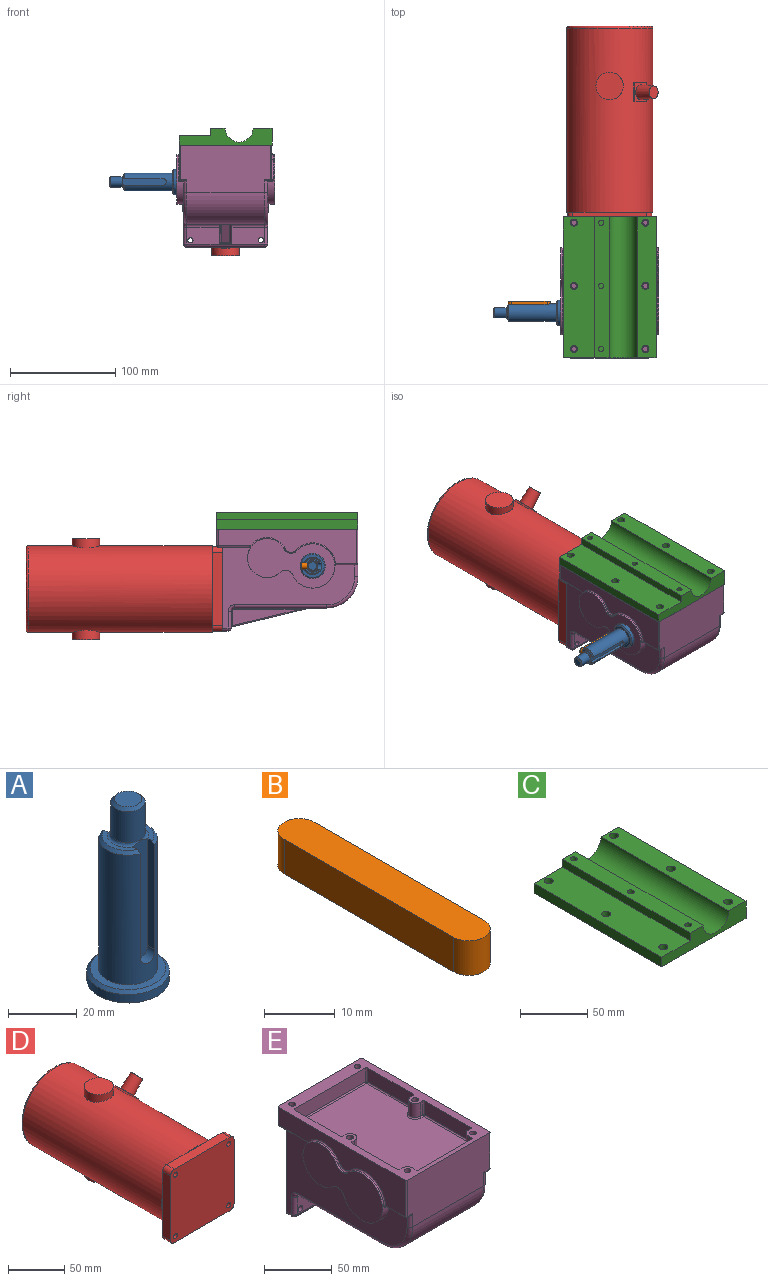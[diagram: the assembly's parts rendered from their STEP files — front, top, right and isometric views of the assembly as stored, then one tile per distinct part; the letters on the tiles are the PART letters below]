
ASSEMBLY  parts=5 mates=4
PART A: 21 faces, bbox 24x24x64 mm
  f0: plane 13.75x4.5mm, normal (0,0,1), area 22.7mm2, adj f10,f14,f18,f20
  f1: plane 13.75x4.5mm, normal (0,0,1), area 22.7mm2, adj f2,f12,f16,f20
  f2: cone r=7.5mm half-angle=45deg, axis (0,0,-1), area 26.8mm2, adj f1,f6,f12,f16
  f3: plane 24x24mm, normal (0,0,-1), area 452.4mm2, adj f4
  f4: cylinder r=12mm len=24mm, axis (0,0,1), area 226.2mm2, adj f3,f9
  f5: plane 22x22mm, normal (0,0,1), area 153.2mm2, adj f6,f9
  f6: cylinder r=8.5mm len=46mm, axis (0,0,1), area 1974.2mm2, adj f2,f5,f10,f12,f13,f14,f16,f17
  f7: cylinder r=4.98mm len=11mm, axis (0,0,1), area 344.2mm2, adj f11,f20
  f8: plane 7.96x7.96mm, normal (0,0,1), area 49.8mm2, adj f11
  f9: cone r=11mm half-angle=45deg, axis (0,0,-1), area 102.2mm2, adj f4,f5
  f10: cone r=7.5mm half-angle=45deg, axis (0,0,-1), area 26.8mm2, adj f0,f6,f14,f18
  f11: cone r=3.98mm half-angle=45deg, axis (0,0,-1), area 39.8mm2, adj f7,f8
  f12: plane 38.04x2.98mm, normal (1,0,0), area 111.7mm2, adj f1,f2,f6,f13,f15,f20
  f13: cylinder r=3mm len=6mm, axis (0,1,0), area 30.4mm2, adj f6,f12,f14,f15
  f14: plane 38.04x2.98mm, normal (-1,0,0), area 111.7mm2, adj f0,f6,f10,f13,f15,f20
  f15: plane 41.8x6mm, normal (0,-1,0), area 244.4mm2, adj f12,f13,f14,f20
  f16: plane 38.04x2.98mm, normal (1,0,0), area 111.7mm2, adj f1,f2,f6,f17,f19,f20
  f17: cylinder r=3mm len=6mm, axis (0,-1,0), area 30.4mm2, adj f6,f16,f18,f19
  f18: plane 38.04x2.98mm, normal (-1,0,0), area 111.7mm2, adj f0,f6,f10,f17,f19,f20
  f19: plane 41.8x6mm, normal (0,1,0), area 244.4mm2, adj f16,f17,f18,f20
  f20: torus R=5.98mm, axis (0,0,1), area 42.4mm2, adj f0,f1,f7,f12,f14,f15,f16,f18
PART B: 6 faces, bbox 6x40x6 mm
  f0: cylinder r=3mm len=6mm, axis (0,0,-1), area 56.5mm2, adj f1,f3,f4,f5
  f1: plane 34x6mm, normal (1,0,0), area 204mm2, adj f0,f2,f4,f5
  f2: cylinder r=3mm len=6mm, axis (0,0,-1), area 56.5mm2, adj f1,f3,f4,f5
  f3: plane 34x6mm, normal (-1,0,0), area 204mm2, adj f0,f2,f4,f5
  f4: plane 40x6mm, normal (0,0,1), area 232.3mm2, adj f0,f1,f2,f3
  f5: plane 40x6mm, normal (0,0,-1), area 232.3mm2, adj f0,f1,f2,f3
PART C: 22 faces, bbox 88.3x134x15.9 mm
  f0: plane 134x15.88mm, normal (1,0,0), area 2127.2mm2, adj f1,f7,f8,f9
  f1: plane 134x88.25mm, normal (0,0,-1), area 11614mm2, adj f0,f2,f8,f9,f16,f17,f18,f19
  f2: plane 134x8.8mm, normal (-1,0,0), area 1179.2mm2, adj f1,f3,f8,f9
  f3: plane 134x29.8mm, normal (0,0,1), area 3887.4mm2, adj f2,f4,f8,f9,f19,f20,f21
  f4: plane 134x7.08mm, normal (-1,0,0), area 948mm2, adj f3,f5,f8,f9
  f5: plane 134x13.75mm, normal (0,0,1), area 1783.6mm2, adj f4,f6,f8,f9,f10,f12,f14
  f6: cylinder r=13.36mm len=134mm, axis (0,1,0), area 5520.3mm2, adj f5,f7,f8,f9
  f7: plane 134x18mm, normal (0,0,1), area 2306.2mm2, adj f0,f6,f8,f9,f16,f17,f18
  f8: plane 88.25x15.88mm, normal (0,-1,0), area 920.1mm2, adj f0,f1,f2,f3,f4,f5,f6,f7
  f9: plane 88.25x15.88mm, normal (0,1,0), area 920.1mm2, adj f0,f1,f2,f3,f4,f5,f6,f7
  f10: cylinder r=2.5mm len=7.08mm, axis (0,0,-1), area 111.1mm2, adj f5,f11
  f11: plane 5x5mm, normal (0,0,1), area 19.6mm2, adj f10
  f12: cylinder r=2.5mm len=7.08mm, axis (0,0,-1), area 111.1mm2, adj f5,f13
  f13: plane 5x5mm, normal (0,0,1), area 19.6mm2, adj f12
  f14: cylinder r=2.5mm len=7.08mm, axis (0,0,-1), area 111.1mm2, adj f5,f15
  f15: plane 5x5mm, normal (0,0,1), area 19.6mm2, adj f14
  f16: cylinder r=3.35mm len=15.88mm, axis (0,0,1), area 334.1mm2, adj f1,f7
  f17: cylinder r=3.35mm len=15.88mm, axis (0,0,1), area 334.1mm2, adj f1,f7
  f18: cylinder r=3.35mm len=15.88mm, axis (0,0,1), area 334.1mm2, adj f1,f7
  f19: cylinder r=3.35mm len=8.8mm, axis (0,0,1), area 185.2mm2, adj f1,f3
  f20: cylinder r=3.35mm len=8.8mm, axis (0,0,1), area 185.2mm2, adj f1,f3
  f21: cylinder r=3.35mm len=8.8mm, axis (0,0,1), area 185.2mm2, adj f1,f3
PART D: 35 faces, bbox 90.4x187x96 mm
  f0: cylinder r=41mm len=175mm, axis (0,-1,0), area 43714.5mm2, adj f1,f2,f3,f12,f14,f15,f16,f18
  f1: plane 31x31mm, normal (0,1,0), area 266.8mm2, adj f0,f4,f7,f11,f33
  f2: plane 31x31mm, normal (0,1,0), area 266.8mm2, adj f0,f6,f8,f11,f32
  f3: plane 31x31mm, normal (0,1,0), area 266.8mm2, adj f0,f5,f6,f9,f31
  f4: plane 70x10mm, normal (1,0,0), area 700mm2, adj f1,f12,f13,f16,f30,f33
  f5: plane 70x10mm, normal (0,0,-1), area 700mm2, adj f3,f12,f13,f18,f30,f31
  f6: plane 70x10mm, normal (-1,0,0), area 700mm2, adj f2,f3,f13,f15,f31,f32
  f7: cylinder r=2.5mm len=10mm, axis (0,-1,0), area 157.1mm2, adj f1,f13
  f8: cylinder r=2.5mm len=10mm, axis (0,-1,0), area 157.1mm2, adj f2,f13
  f9: cylinder r=2.5mm len=10mm, axis (0,-1,0), area 157.1mm2, adj f3,f13
  f10: cylinder r=2.5mm len=10mm, axis (0,-1,0), area 157.1mm2, adj f12,f13
  f11: plane 70x10mm, normal (0,0,1), area 700mm2, adj f1,f2,f13,f14,f32,f33
  f12: plane 31x31mm, normal (0,1,0), area 266.8mm2, adj f0,f4,f5,f10,f30
  f13: plane 80x80mm, normal (0,-1,0), area 6300mm2, adj f4,f5,f6,f7,f8,f9,f10,f11
  f14: plane 18x1mm, normal (0,-1,0), area 12mm2, adj f0,f11
  f15: plane 18x1mm, normal (0,-1,0), area 12mm2, adj f0,f6
  f16: plane 18x1mm, normal (0,-1,0), area 12mm2, adj f0,f4
  f17: plane 78x78mm, normal (0,1,0), area 4778.4mm2, adj f34
  f18: plane 18x1mm, normal (0,-1,0), area 12mm2, adj f0,f5
  f19: plane 26x26mm, normal (0,0,1), area 530.9mm2, adj f20
  f20: cylinder r=13mm len=26mm, axis (0,0,-1), area 657.6mm2, adj f0,f19
  f21: cylinder r=13mm len=26mm, axis (0,0,-1), area 657.6mm2, adj f0,f22
  f22: plane 26x26mm, normal (0,0,-1), area 530.9mm2, adj f21
  f23: plane 18x1.26mm, normal (-0.71,0,0.71), area 32.2mm2, adj f0,f25,f26,f27
  f24: plane 18x1.26mm, normal (0.71,0,-0.71), area 32.2mm2, adj f0,f25,f26,f27
  f25: plane 12.58x12.58mm, normal (0,1,0), area 20.2mm2, adj f0,f23,f24,f27
  f26: plane 12.58x12.58mm, normal (0,-1,0), area 20.2mm2, adj f0,f23,f24,f27
  f27: plane 18x11.31mm, normal (0.71,0,0.71), area 134.1mm2, adj f23,f24,f25,f26,f28
  f28: cone r=7mm half-angle=3deg, axis (-0.71,0,-0.71), area 701.1mm2, adj f27,f29
  f29: plane 12.22x8.64mm, normal (0.71,0,0.71), area 117.2mm2, adj f28
  f30: cylinder r=5mm len=10mm, axis (0,-1,0), area 78.5mm2, adj f4,f5,f12,f13
  f31: cylinder r=5mm len=10mm, axis (0,1,0), area 78.5mm2, adj f3,f5,f6,f13
  f32: cylinder r=5mm len=10mm, axis (0,-1,0), area 78.5mm2, adj f2,f6,f11,f13
  f33: cylinder r=5mm len=10mm, axis (0,1,0), area 78.5mm2, adj f1,f4,f11,f13
  f34: torus R=39mm, axis (0,1,0), area 795mm2, adj f0,f17
PART E: 163 faces, bbox 93x136.5x97 mm
  f0: cylinder r=3mm len=31mm, axis (1,0,0), area 146.1mm2, adj f3,f10,f45,f150
  f1: plane 134x88mm, normal (0,0,1), area 2921.3mm2, adj f2,f24,f25,f26,f48,f57,f64,f69
  f2: plane 86x45mm, normal (0,-1,0), area 3726mm2, adj f1,f31,f32,f34,f48,f49,f56,f57
  f3: plane 87.5x74mm, normal (0,0,-1), area 5616.9mm2, adj f0,f31,f35,f41,f42,f149,f151,f154
  f4: plane 80x80mm, normal (0,1,0), area 6317.6mm2, adj f5,f6,f7,f8,f9,f11,f13,f23
  f5: plane 125.5x77mm, normal (1,0,0), area 4068.3mm2, adj f4,f19,f20,f21,f22,f23,f32,f33
  f6: plane 125.5x77mm, normal (-1,0,0), area 4068.3mm2, adj f4,f15,f16,f17,f18,f23,f34,f38
  f7: plane 74x5mm, normal (0,0,-1), area 370mm2, adj f4,f37,f43,f44
  f8: cylinder r=2.5mm len=8mm, axis (0,1,0), area 125.7mm2, adj f4,f10
  f9: cylinder r=2.5mm len=8mm, axis (0,1,0), area 125.7mm2, adj f4,f10
  f10: plane 74x16mm, normal (0,-1,0), area 957mm2, adj f0,f8,f9,f36,f42,f43,f47,f152
  f11: cylinder r=2.5mm len=6mm, axis (0,1,0), area 94.2mm2, adj f4,f12
  f12: plane 5x5mm, normal (0,1,0), area 19.6mm2, adj f11
  f13: cylinder r=2.5mm len=6mm, axis (0,1,0), area 94.2mm2, adj f4,f14
  f14: plane 5x5mm, normal (0,1,0), area 19.6mm2, adj f13
  f15: plane 20x3.76mm, normal (0,0,-1), area 60.5mm2, adj f6,f34,f49,f51,f52
  f16: cylinder r=21mm len=42mm, axis (-1,0,0), area 449.8mm2, adj f6,f17,f27,f28,f52,f53,f54
  f17: cylinder r=7.11mm len=11.42mm, axis (-1,0,0), area 88.9mm2, adj f6,f16,f18,f27
  f18: cylinder r=18.5mm len=37mm, axis (-1,0,0), area 402.3mm2, adj f6,f17,f27,f28,f58,f59,f61
  f19: plane 20x3.76mm, normal (0,0,-1), area 60.5mm2, adj f5,f32,f56,f62,f63
  f20: cylinder r=21mm len=42mm, axis (-1,0,0), area 449.8mm2, adj f5,f21,f29,f30,f62,f66,f68
  f21: cylinder r=7.11mm len=11.42mm, axis (-1,0,0), area 88.9mm2, adj f5,f20,f22,f30
  f22: cylinder r=18.5mm len=37mm, axis (-1,0,0), area 402.3mm2, adj f5,f21,f29,f30,f73,f75,f76
  f23: plane 86x29.51mm, normal (0,0,-1), area 537.1mm2, adj f4,f5,f6,f59,f65,f70,f74,f76
  f24: plane 86x16mm, normal (0,1,0), area 1376mm2, adj f1,f64,f69,f70
  f25: plane 132x33mm, normal (1,0,0), area 2354mm2, adj f1,f57,f63,f68,f69,f71,f73,f74
  f26: plane 132x33mm, normal (-1,0,0), area 2354mm2, adj f1,f48,f51,f54,f55,f58,f64,f65
  f27: plane 82.96x47mm, normal (-1,0,0), area 2565.2mm2, adj f16,f17,f18,f28
  f28: cylinder r=7.11mm len=11.55mm, axis (-1,0,0), area 20.5mm2, adj f16,f18,f27,f55
  f29: cylinder r=7.11mm len=11.55mm, axis (-1,0,0), area 20.5mm2, adj f20,f22,f30,f71
  f30: plane 82.96x47mm, normal (1,0,0), area 2565.2mm2, adj f20,f21,f22,f29
  f31: cylinder r=30mm len=74mm, axis (1,0,0), area 3487.2mm2, adj f2,f3,f33,f38
  f32: cylinder r=3mm len=12mm, axis (0,0,1), area 53.1mm2, adj f2,f5,f19,f33,f56
  f33: torus R=27mm, axis (1,0,0), area 214mm2, adj f5,f31,f32,f35
  f34: cylinder r=3mm len=12mm, axis (0,0,-1), area 53.1mm2, adj f2,f6,f15,f38,f49
  f35: cylinder r=3mm len=87.5mm, axis (0,-1,0), area 412.3mm2, adj f3,f5,f33,f39
  f36: cylinder r=3mm len=16mm, axis (0,0,-1), area 75.4mm2, adj f5,f10,f39,f40
  f37: cylinder r=3mm len=5mm, axis (0,-1,0), area 23.6mm2, adj f4,f5,f7,f40
  f38: torus R=27mm, axis (1,0,0), area 214mm2, adj f6,f31,f34,f41
  f39: torus R=6mm, axis (1,0,0), area 30.3mm2, adj f5,f35,f36,f42
  f40: sphere r=3mm, area 14.1mm2, adj f36,f37,f43
  f41: cylinder r=3mm len=87.5mm, axis (0,1,0), area 412.3mm2, adj f3,f6,f38,f45
  f42: cylinder r=3mm len=31mm, axis (1,0,0), area 146.1mm2, adj f3,f10,f39,f160
  f43: cylinder r=3mm len=74mm, axis (-1,0,0), area 348.7mm2, adj f7,f10,f40,f46
  f44: cylinder r=3mm len=5mm, axis (0,1,0), area 23.6mm2, adj f4,f6,f7,f46
  f45: torus R=6mm, axis (1,0,0), area 30.3mm2, adj f0,f6,f41,f47
  f46: sphere r=3mm, area 14.1mm2, adj f43,f44,f47
  f47: cylinder r=3mm len=16mm, axis (0,0,1), area 75.4mm2, adj f6,f10,f45,f46
  f48: cylinder r=1mm len=33mm, axis (0,0,-1), area 51.8mm2, adj f1,f2,f26,f50
  f49: cylinder r=1mm len=6mm, axis (-1,0,0), area 7.7mm2, adj f2,f15,f34,f50
  f50: sphere r=1mm, area 1.6mm2, adj f48,f49,f51
  f51: cylinder r=1mm len=20.09mm, axis (0,1,0), area 31.5mm2, adj f15,f26,f50,f53
  f52: cylinder r=1mm len=3mm, axis (-1,0,0), area 4.7mm2, adj f6,f15,f16,f53
  f53: bspline ~2.45x2.23mm, area 3.3mm2, adj f16,f51,f52,f54
  f54: torus R=22mm, axis (1,0,0), area 77.3mm2, adj f16,f26,f53,f55
  f55: torus R=6.11mm, axis (1,0,0), area 20.4mm2, adj f26,f28,f54,f58
  f56: cylinder r=1mm len=6mm, axis (-1,0,0), area 7.7mm2, adj f2,f19,f32,f60
  f57: cylinder r=1mm len=33mm, axis (0,0,1), area 51.8mm2, adj f1,f2,f25,f60
  f58: torus R=19.5mm, axis (1,0,0), area 60.5mm2, adj f18,f26,f55,f61
  f59: cylinder r=1mm len=3mm, axis (-1,0,0), area 6.2mm2, adj f6,f18,f23,f61
  f60: sphere r=1mm, area 1.6mm2, adj f56,f57,f63
  f61: bspline ~2.77x2.49mm, area 4.3mm2, adj f18,f58,f59,f65
  f62: cylinder r=1mm len=3mm, axis (-1,0,0), area 4.7mm2, adj f5,f19,f20,f66
  f63: cylinder r=1mm len=20.09mm, axis (0,-1,0), area 31.5mm2, adj f19,f25,f60,f66
  f64: cylinder r=1mm len=16mm, axis (0,0,1), area 25.1mm2, adj f1,f24,f26,f67
  f65: cylinder r=1mm len=30.79mm, axis (0,1,0), area 47.1mm2, adj f23,f26,f61,f67
  f66: bspline ~2.34x2.34mm, area 3.3mm2, adj f20,f62,f63,f68
  f67: sphere r=1mm, area 1.6mm2, adj f64,f65,f70
  f68: torus R=22mm, axis (1,0,0), area 77.3mm2, adj f20,f25,f66,f71
  f69: cylinder r=1mm len=16mm, axis (0,0,-1), area 25.1mm2, adj f1,f24,f25,f72
  f70: cylinder r=1mm len=86mm, axis (-1,0,0), area 135.1mm2, adj f23,f24,f67,f72
  f71: torus R=6.11mm, axis (1,0,0), area 20.4mm2, adj f25,f29,f68,f73
  f72: sphere r=1mm, area 1.6mm2, adj f69,f70,f74
  f73: torus R=19.5mm, axis (1,0,0), area 60.5mm2, adj f22,f25,f71,f75
  f74: cylinder r=1mm len=30.79mm, axis (0,-1,0), area 47.1mm2, adj f23,f25,f72,f75
  f75: bspline ~2.7x2.4mm, area 4.3mm2, adj f22,f73,f74,f76
  f76: cylinder r=1mm len=3mm, axis (-1,0,0), area 6.2mm2, adj f5,f22,f23,f75
  f77: plane 56x12.5mm, normal (0,1,0), area 700mm2, adj f1,f139,f143,f145
  f78: plane 12.5x4mm, normal (-1,0,0), area 50mm2, adj f1,f79,f138,f139
  f79: cylinder r=5mm len=12.5mm, axis (0,0,1), area 98.2mm2, adj f1,f78,f80,f136
  f80: plane 12.5x3mm, normal (0,1,0), area 37.5mm2, adj f1,f79,f129,f134
  f81: plane 48x12.5mm, normal (-1,0,0), area 600mm2, adj f1,f123,f128,f129
  f82: plane 12.5x3mm, normal (0,-1,0), area 37.5mm2, adj f1,f83,f122,f123
  f83: cylinder r=5mm len=12.5mm, axis (0,0,1), area 196.3mm2, adj f1,f82,f84,f120
  f84: plane 12.5x3mm, normal (0,1,0), area 37.5mm2, adj f1,f83,f113,f118
  f85: plane 47.5x12.5mm, normal (-1,0,0), area 593.8mm2, adj f1,f108,f112,f113
  f86: plane 74x12.5mm, normal (0,-1,0), area 925mm2, adj f1,f108,f110,f111
  f87: plane 47.5x12.5mm, normal (1,0,0), area 593.8mm2, adj f1,f110,f116,f117
  f88: plane 12.5x3mm, normal (0,1,0), area 37.5mm2, adj f1,f89,f116,f121
  f89: cylinder r=5mm len=12.5mm, axis (0,0,1), area 196.3mm2, adj f1,f88,f90,f124
  f90: plane 12.5x3mm, normal (0,-1,0), area 37.5mm2, adj f1,f89,f126,f127
  f91: plane 48x12.5mm, normal (1,0,0), area 600mm2, adj f1,f126,f132,f133
  f92: plane 12.5x3mm, normal (0,1,0), area 37.5mm2, adj f1,f93,f132,f137
  f93: cylinder r=5mm len=12.5mm, axis (0,0,1), area 98.2mm2, adj f1,f92,f94,f140
  f94: plane 12.5x4mm, normal (1,0,0), area 50mm2, adj f1,f93,f142,f145
  f95: plane 117.5x74mm, normal (0,0,1), area 8345.4mm2, adj f111,f112,f117,f118,f120,f121,f122,f124
  f96: cylinder r=2.5mm len=13.5mm, axis (0,0,1), area 212.1mm2, adj f1,f97
  f97: plane 5x5mm, normal (0,0,1), area 19.6mm2, adj f96
  f98: cylinder r=2.5mm len=13.5mm, axis (0,0,1), area 212.1mm2, adj f1,f99
  f99: plane 5x5mm, normal (0,0,1), area 19.6mm2, adj f98
  f100: cylinder r=2.5mm len=13.5mm, axis (0,0,1), area 212.1mm2, adj f1,f101
  f101: plane 5x5mm, normal (0,0,1), area 19.6mm2, adj f100
  f102: cylinder r=2.5mm len=13.5mm, axis (0,0,1), area 212.1mm2, adj f1,f103
  f103: plane 5x5mm, normal (0,0,1), area 19.6mm2, adj f102
  f104: cylinder r=2.5mm len=13.5mm, axis (0,0,1), area 212.1mm2, adj f1,f105
  f105: plane 5x5mm, normal (0,0,1), area 19.6mm2, adj f104
  f106: cylinder r=2.5mm len=13.5mm, axis (0,0,1), area 212.1mm2, adj f1,f107
  f107: plane 5x5mm, normal (0,0,1), area 19.6mm2, adj f106
  f108: cylinder r=1mm len=12.5mm, axis (0,0,1), area 19.6mm2, adj f1,f85,f86,f109
  f109: sphere r=1mm, area 1.6mm2, adj f108,f111,f112
  f110: cylinder r=1mm len=12.5mm, axis (0,0,-1), area 19.6mm2, adj f1,f86,f87,f114
  f111: cylinder r=1mm len=74mm, axis (-1,0,0), area 116.2mm2, adj f86,f95,f109,f114
  f112: cylinder r=1mm len=47.5mm, axis (0,1,0), area 74.6mm2, adj f85,f95,f109,f115
  f113: cylinder r=1mm len=12.5mm, axis (0,0,1), area 19.6mm2, adj f1,f84,f85,f115
  f114: sphere r=1mm, area 1.6mm2, adj f110,f111,f117
  f115: sphere r=1mm, area 1.6mm2, adj f112,f113,f118
  f116: cylinder r=1mm len=12.5mm, axis (0,0,1), area 19.6mm2, adj f1,f87,f88,f119
  f117: cylinder r=1mm len=47.5mm, axis (0,-1,0), area 74.6mm2, adj f87,f95,f114,f119
  f118: cylinder r=1mm len=3mm, axis (1,0,0), area 4.7mm2, adj f84,f95,f115,f120
  f119: sphere r=1mm, area 1.6mm2, adj f116,f117,f121
  f120: torus R=6mm, axis (0,0,1), area 26.5mm2, adj f83,f95,f118,f122
  f121: cylinder r=1mm len=3mm, axis (1,0,0), area 4.7mm2, adj f88,f95,f119,f124
  f122: cylinder r=1mm len=3mm, axis (-1,0,0), area 4.7mm2, adj f82,f95,f120,f125
  f123: cylinder r=1mm len=12.5mm, axis (0,0,-1), area 19.6mm2, adj f1,f81,f82,f125
  f124: torus R=6mm, axis (0,0,1), area 26.5mm2, adj f89,f95,f121,f127
  f125: sphere r=1mm, area 1.6mm2, adj f122,f123,f128
  f126: cylinder r=1mm len=12.5mm, axis (0,0,-1), area 19.6mm2, adj f1,f90,f91,f130
  f127: cylinder r=1mm len=3mm, axis (-1,0,0), area 4.7mm2, adj f90,f95,f124,f130
  f128: cylinder r=1mm len=48mm, axis (0,1,0), area 75.4mm2, adj f81,f95,f125,f131
  f129: cylinder r=1mm len=12.5mm, axis (0,0,1), area 19.6mm2, adj f1,f80,f81,f131
  f130: sphere r=1mm, area 1.6mm2, adj f126,f127,f133
  f131: sphere r=1mm, area 1.6mm2, adj f128,f129,f134
  f132: cylinder r=1mm len=12.5mm, axis (0,0,1), area 19.6mm2, adj f1,f91,f92,f135
  f133: cylinder r=1mm len=48mm, axis (0,-1,0), area 75.4mm2, adj f91,f95,f130,f135
  f134: cylinder r=1mm len=3mm, axis (1,0,0), area 4.7mm2, adj f80,f95,f131,f136
  f135: sphere r=1mm, area 1.6mm2, adj f132,f133,f137
  f136: torus R=6mm, axis (0,0,1), area 13.2mm2, adj f79,f95,f134,f138
  f137: cylinder r=1mm len=3mm, axis (1,0,0), area 4.7mm2, adj f92,f95,f135,f140
  f138: cylinder r=1mm len=4mm, axis (0,1,0), area 6.3mm2, adj f78,f95,f136,f141
  f139: cylinder r=1mm len=12.5mm, axis (0,0,-1), area 19.6mm2, adj f1,f77,f78,f141
  f140: torus R=6mm, axis (0,0,1), area 13.2mm2, adj f93,f95,f137,f142
  f141: sphere r=1mm, area 1.6mm2, adj f138,f139,f143
  f142: cylinder r=1mm len=4mm, axis (0,-1,0), area 6.3mm2, adj f94,f95,f140,f144
  f143: cylinder r=1mm len=56mm, axis (1,0,0), area 88mm2, adj f77,f95,f141,f144
  f144: sphere r=1mm, area 1.6mm2, adj f142,f143,f145
  f145: cylinder r=1mm len=12.5mm, axis (0,0,1), area 19.6mm2, adj f1,f77,f94,f144
  f146: plane 65.55x15.73mm, normal (1,0,0), area 514.7mm2, adj f157,f159,f160,f162
  f147: plane 65.55x15.73mm, normal (-1,0,0), area 514.7mm2, adj f149,f150,f152,f153
  f148: plane 74.12x17.79mm, normal (0,-0.23,-0.97), area 609.8mm2, adj f153,f154,f158,f159
  f149: cylinder r=1mm len=63.55mm, axis (0,1,0), area 99.8mm2, adj f3,f147,f150,f151
  f150: torus R=2mm, axis (1,0,0), area 6.5mm2, adj f0,f147,f149,f152
  f151: bspline ~8.57x2mm, area 8.8mm2, adj f3,f149,f153,f154
  f152: cylinder r=1mm len=13.73mm, axis (0,0,-1), area 21.6mm2, adj f10,f147,f150,f155
  f153: cylinder r=1mm len=74.35mm, axis (0,0.97,-0.23), area 114.6mm2, adj f147,f148,f151,f155
  f154: cylinder r=1mm len=8mm, axis (1,0,0), area 1.9mm2, adj f3,f148,f151,f156
  f155: bspline ~2.14x2.06mm, area 3.2mm2, adj f10,f152,f153,f158
  f156: bspline ~8.57x2mm, area 8.8mm2, adj f3,f154,f157,f159
  f157: cylinder r=1mm len=63.55mm, axis (0,-1,0), area 99.8mm2, adj f3,f146,f156,f160
  f158: cylinder r=1mm len=8mm, axis (1,0,0), area 10.7mm2, adj f10,f148,f155,f161
  f159: cylinder r=1mm len=74.35mm, axis (0,-0.97,0.23), area 114.6mm2, adj f146,f148,f156,f161
  f160: torus R=2mm, axis (1,0,0), area 6.5mm2, adj f42,f146,f157,f162
  f161: bspline ~2.41x2.35mm, area 3.2mm2, adj f10,f158,f159,f162
  f162: cylinder r=1mm len=13.73mm, axis (0,0,1), area 21.6mm2, adj f10,f146,f160,f161
PLACE A rot(axis=(0,-1,0),90deg) t=(-46.5,-85.5,22)mm
PLACE B rot(axis=(-0.58,0.58,0.58),120deg) t=(-76.5,-80.5,22)mm
PLACE C at identity
PLACE D t=(0,0,0.02)mm
PLACE E at identity fixed
MATE fastened C.f16 <-> E.f79  axis (0,0,-1) through (34,-120,57)mm
MATE revolute A.f9 <-> E.f16  axis (1,0,0) through (-46.5,-85.5,22)mm
MATE fastened B.f0 <-> A.f13  axis (0,-1,0) through (-59.5,-80.5,22)mm
MATE fastened E.f4 <-> D.f0  axis (0,1,0) through (0,0,0.02)mm
